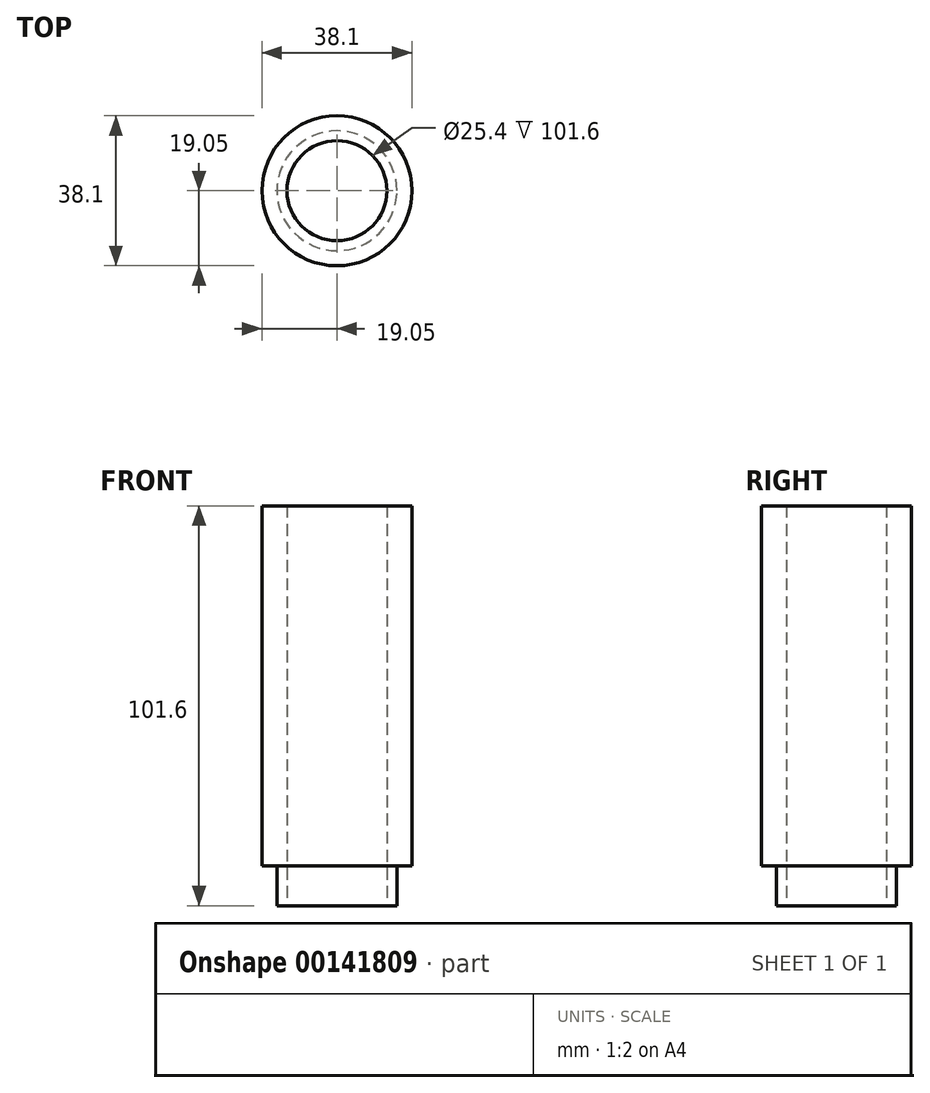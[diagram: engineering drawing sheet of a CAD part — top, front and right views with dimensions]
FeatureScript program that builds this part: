
annotation { "Feature Type Name" : "Feature", "Feature Type Description" : "" }
export const myFeature = defineFeature(function(context is Context, id is Id, definition is map)
    precondition{}
    {
        {
            var Q0;
            Q0=qCreatedBy(makeId("Top.planeOp"),FACE);
            var sketch = newSketch(context, id + "F0", { "sketchPlane" : qUnion([Q0])});
            skCircle(sketch, "E0", {"center": v(0, 0) * mm, "radius": 19.05 * mm});
            skSolve(sketch);
        }
        {
            var Q0;
            Q0=makeQuery(id+"F0.imprint","IMPRINT",FACE,{"disambiguationData":[TD([[makeQuery(id+"F0.imprint","IMPRINT",EDGE,{"derivedFrom":sQuery(id+"F0.wireOp",EDGE,"E0")}),1.0]])]});
            var sketch = newSketch(context, id + "F1", { "sketchPlane" : qUnion([Q0])});
            skCircle(sketch, "E1", {"center": v(0, 0) * mm, "radius": 12.7 * mm});
            skSolve(sketch);
        }
        {
            var Q0;
            Q0=makeQuery(id+"F1.imprint","IMPRINT",FACE,{"disambiguationData":[TD([[makeQuery(id+"F1.imprint","IMPRINT",EDGE,{"derivedFrom":sQuery(id+"F1.wireOp",EDGE,"E1")}),-1.0]])]});
            extrude(context, id + "F2", {"entities" : qUnion([Q0]), "depth" : 101.6 * mm});
        }
        {
            var Q0;
            Q0=makeQuery(id+"F0.imprint","IMPRINT",FACE,{"disambiguationData":[TD([[makeQuery(id+"F0.imprint","IMPRINT",EDGE,{"derivedFrom":sQuery(id+"F0.wireOp",EDGE,"E0")}),1.0]])]});
            var sketch = newSketch(context, id + "F3", { "sketchPlane" : qUnion([Q0])});
            skCircle(sketch, "E2", {"center": v(0, 0) * mm, "radius": 15.24 * mm});
            skSolve(sketch);
        }
        {
            var Q0;
            Q0=makeQuery(id+"F3.imprint","IMPRINT",FACE,{"disambiguationData":[TD([[makeQuery(id+"F3.imprint","IMPRINT",EDGE,{"derivedFrom":sQuery(id+"F3.wireOp",EDGE,"E2")}),-1.0]])]});
            extrude(context, id + "F4", {"entities" : qUnion([Q0]), "operationType" : NewBodyOperationType.REMOVE, "depth" : 10.16 * mm});
        }
    });
